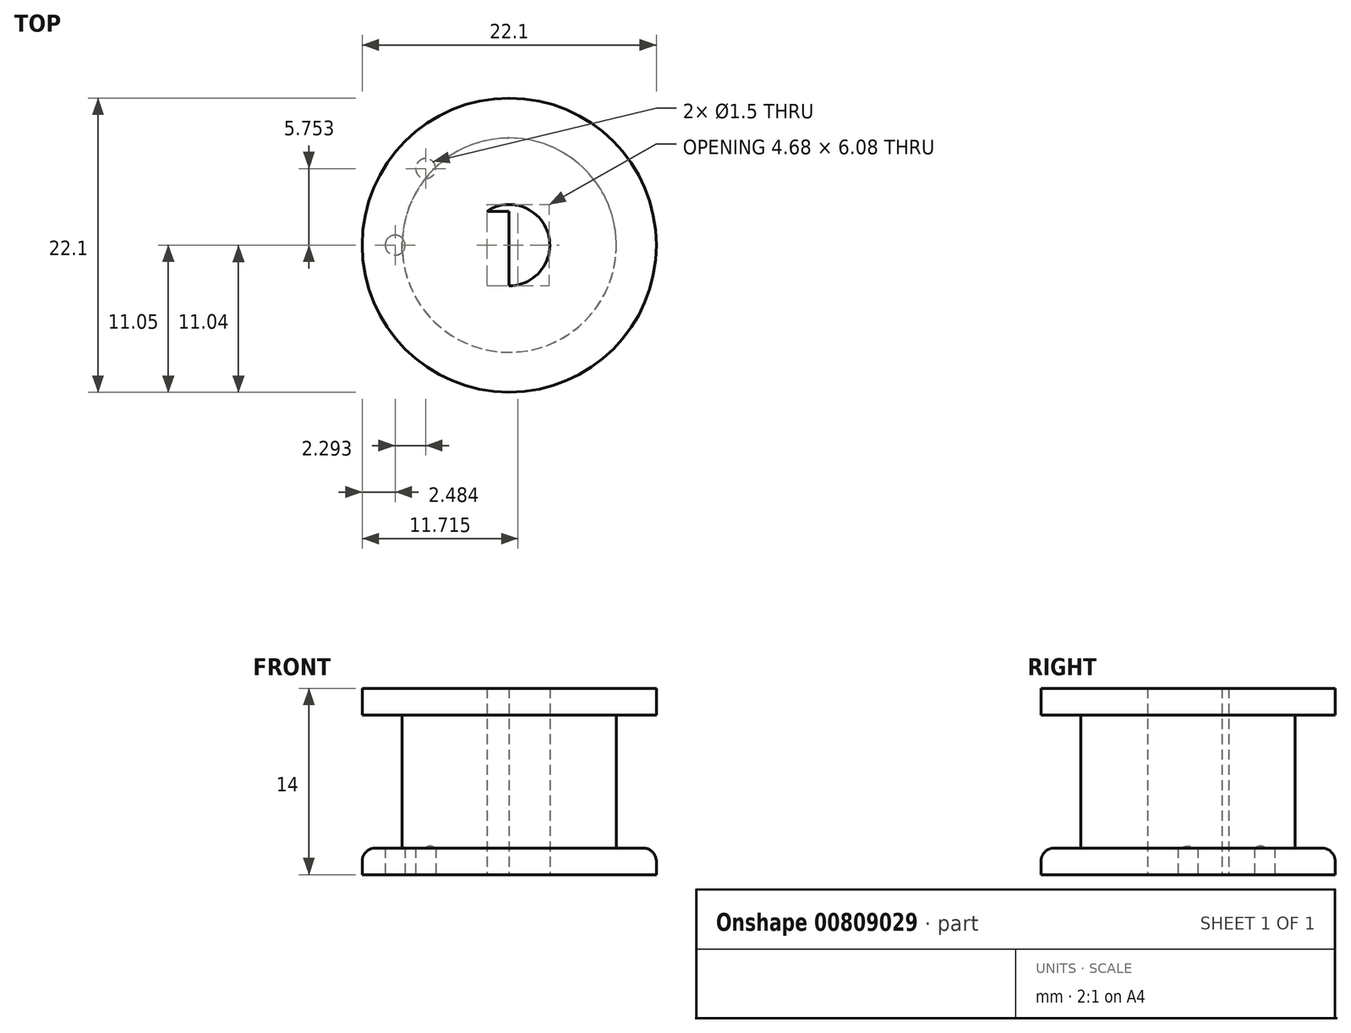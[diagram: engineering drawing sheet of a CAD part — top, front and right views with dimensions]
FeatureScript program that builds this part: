
annotation { "Feature Type Name" : "Feature", "Feature Type Description" : "" }
export const myFeature = defineFeature(function(context is Context, id is Id, definition is map)
    precondition{}
    {
        {
            var Q0;
            Q0=qCreatedBy(makeId("Top.planeOp"),FACE);
            var sketch = newSketch(context, id + "F0", { "sketchPlane" : qUnion([Q0])});
            skCircle(sketch, "E0", {"center": v(0, 0) * mm, "radius": 3.05 * mm});
            skLineSegment(sketch, "E1", {"start": v(0, -3.05) * mm, "end": v(0, 2.55) * mm});
            skLineSegment(sketch, "E2", {"start": v(0, 2.55) * mm, "end": v(1.67, 2.55) * mm});
            skLineSegment(sketch, "E3", {"start": v(1.67, 2.55) * mm, "end": v(-1.67, 2.55) * mm});
            skCircle(sketch, "E4.0", {"center": v(0, 0) * mm, "radius": 8.05 * mm});
            skCircle(sketch, "E5.0", {"center": v(0, 0) * mm, "radius": 11.05 * mm});
            skPoint(sketch, "E6", {"position": v(-8.57, 0) * mm});
            skPoint(sketch, "E7", {"position": v(-6.27, 5.75) * mm});
            skSolve(sketch);
        }
        {
            var Q0;
            Q0=makeQuery(id+"F0.imprint","IMPRINT",FACE,{"disambiguationData":[TD([[makeQuery(id+"F0.imprint","IMPRINT",EDGE,{"derivedFrom":sQuery(id+"F0.wireOp",EDGE,"E4.0")}),1.0]])]});
            var Q1;
            {var subQ0=sQuery(id+"F0.wireOp",EDGE,"E3");var subQ1=sQuery(id+"F0.wireOp",EDGE,"E0");var subQ2=makeQuery(id+"F0.imprint","INTERSECT",VERTEX,{"disambiguationData":[OD(0.0)],"derivedFrom":[subQ1,subQ0]});Q1=makeQuery(id+"F0.imprint","IMPRINT",FACE,{"disambiguationData":[TD([[makeQuery(id+"F0.imprint","IMPRINT",EDGE,{"disambiguationData":[TD([[subQ2,-1.0]])],"derivedFrom":subQ1}),1.0]])]});}
            extrude(context, id + "F1", {"entities" : qUnion([Q0, Q1]), "depth" : 14 * mm, "offsetDistance" : 25 * mm});
        }
        {
            var Q0;
            Q0=makeQuery(id+"F0.imprint","IMPRINT",FACE,{"disambiguationData":[TD([[makeQuery(id+"F0.imprint","IMPRINT",EDGE,{"derivedFrom":sQuery(id+"F0.wireOp",EDGE,"E4.0")}),-1.0]])]});
            extrude(context, id + "F2", {"entities" : qUnion([Q0]), "operationType" : NewBodyOperationType.ADD, "depth" : 14 * mm, "offsetDistance" : 25 * mm});
        }
        {
            var Q0;
            Q0 = qSketchRegion(id + "F0", true);
            extrude(context, id + "F3", {"entities" : qUnion([Q0]), "operationType" : NewBodyOperationType.REMOVE, "depth" : 12 * mm, "offsetDistance" : 25 * mm});
        }
        {
            var Q0;
            Q0=makeQuery(id+"F0.imprint","IMPRINT",FACE,{"disambiguationData":[TD([[makeQuery(id+"F0.imprint","IMPRINT",EDGE,{"derivedFrom":sQuery(id+"F0.wireOp",EDGE,"E4.0")}),-1.0]])]});
            extrude(context, id + "F4", {"entities" : qUnion([Q0]), "operationType" : NewBodyOperationType.ADD, "depth" : 2 * mm, "offsetDistance" : 25 * mm});
        }
        {
            var Q0;
            Q0=makeQuery(id+"F3.boolean.opBoolean","COPY",EDGE,{"derivedFrom":makeQuery(id+"F3.opExtrude","CAP_EDGE",EDGE,{"disambiguationData":[OSD([sQuery(id+"F0.wireOp",EDGE,"E5.0")])],"isStart":false})});
            var Q1;
            Q1=makeQuery(id+"F4.opExtrude","CAP_EDGE",EDGE,{"disambiguationData":[OSD([sQuery(id+"F0.wireOp",EDGE,"E5.0")])],"isStart":false});
            fillet(context, id + "F5", {"entities" : qUnion([Q0, Q1]), "radius" : 1 * mm, "tangentPropagation" : true, "allowEdgeOverflow" : false});
        }
        {
            var Q0;
            Q0=sQuery(id+"F0.wireOp",VERTEX,"E6");
            var Q1;
            Q1=makeQuery(id+"F1.opExtrude","SWEPT_BODY",BODY,{"disambiguationData":[OSD([sQuery(id+"F0.wireOp",EDGE,"E0"),sQuery(id+"F0.wireOp",EDGE,"E3"),sQuery(id+"F0.wireOp",EDGE,"E4.0")])]});
            hole(context, id + "F6", {"style" : HoleStyle.SIMPLE, "endStyle" : HoleEndStyle.BLIND, "oppositeDirection" : true, "holeDiameter" : 1.5 * mm, "majorDiameter" : 5 * mm, "holeDepth" : 2 * mm, "isTappedThrough" : true, "tappedDepth" : 12 * mm, "tapClearance" : 3, "locations" : qUnion([Q0]), "scope" : qUnion([Q1])});
        }
        {
            var Q0;
            Q0=sQuery(id+"F0.wireOp",VERTEX,"E7");
            var Q1;
            Q1=makeQuery(id+"F1.opExtrude","SWEPT_BODY",BODY,{"disambiguationData":[OSD([sQuery(id+"F0.wireOp",EDGE,"E0"),sQuery(id+"F0.wireOp",EDGE,"E3"),sQuery(id+"F0.wireOp",EDGE,"E4.0")])]});
            hole(context, id + "F7", {"style" : HoleStyle.SIMPLE, "endStyle" : HoleEndStyle.BLIND, "oppositeDirection" : true, "holeDiameter" : 1.5 * mm, "majorDiameter" : 5 * mm, "holeDepth" : 2 * mm, "isTappedThrough" : true, "tappedDepth" : 12 * mm, "tapClearance" : 3, "locations" : qUnion([Q0]), "scope" : qUnion([Q1])});
        }
    });
